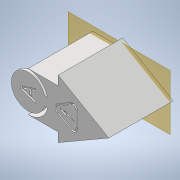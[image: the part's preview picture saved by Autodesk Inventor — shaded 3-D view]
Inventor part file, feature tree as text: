
AUTODESK INVENTOR PART (.ipt)
format: ipt  version: 2022.3 (Build 263350000, 350)  size: 257,024 bytes
history: native  units: mm
features: sketch x6, plane x5, reference x5, extrude x4, other x3, emboss x2
ambient origin geometry x8: Origin, YZ Plane, XZ Plane, XY Plane, X Axis, Y Axis, Z Axis, Center Point
bodies: Solid1 (feature_tree)
feature tree (25):
  sketch  "Sketch1"  dims[d0=10.0mm d1=0.0mm d2=0.2mm]
  other  "Work Point1"
  extrude  "Extrusion1"  Depth=10.0mm
  plane  "Work Plane1"
  sketch  "Sketch2"  dims[d3=1.0mm d4=10.0mm d5=0.0mm]
  plane  "Work Plane2"
  extrude  "Extrusion2"  Depth=10.0mm TaperAngle=0.0deg
  plane  "Work Plane3"
  sketch  "Sketch3"  dims[d6=10.0mm d7=0.0mm d8=2.0mm d9=0.0mm]
  plane  "Work Plane4"
  extrude  "Extrusion3"  Depth=2.0mm TaperAngle=0.0deg
  plane  "Work Plane5"
  extrude  "Extrusion4"  Depth=22.0mm
  emboss  "Emboss1"
  emboss  "Emboss2"
  reference  "Reference1"
  reference  "Reference2"
  reference  "Reference3"
  sketch  "Sketch4"  dims[d10=22.0mm d11=22.0mm]
  reference  "Reference4"
  reference  "Reference5"
  sketch  "Sketch5"  dims[d12=22.0mm]
  sketch  "Sketch6"  dims[d13=22.0mm d14=0.0mm d15=0.0mm d16=1.0mm d17=0.0mm d18=2.0mm d19=1.0mm d20=1.0mm d21=0.0mm]
  other  "Assembly2"
  other  "Base:1"
